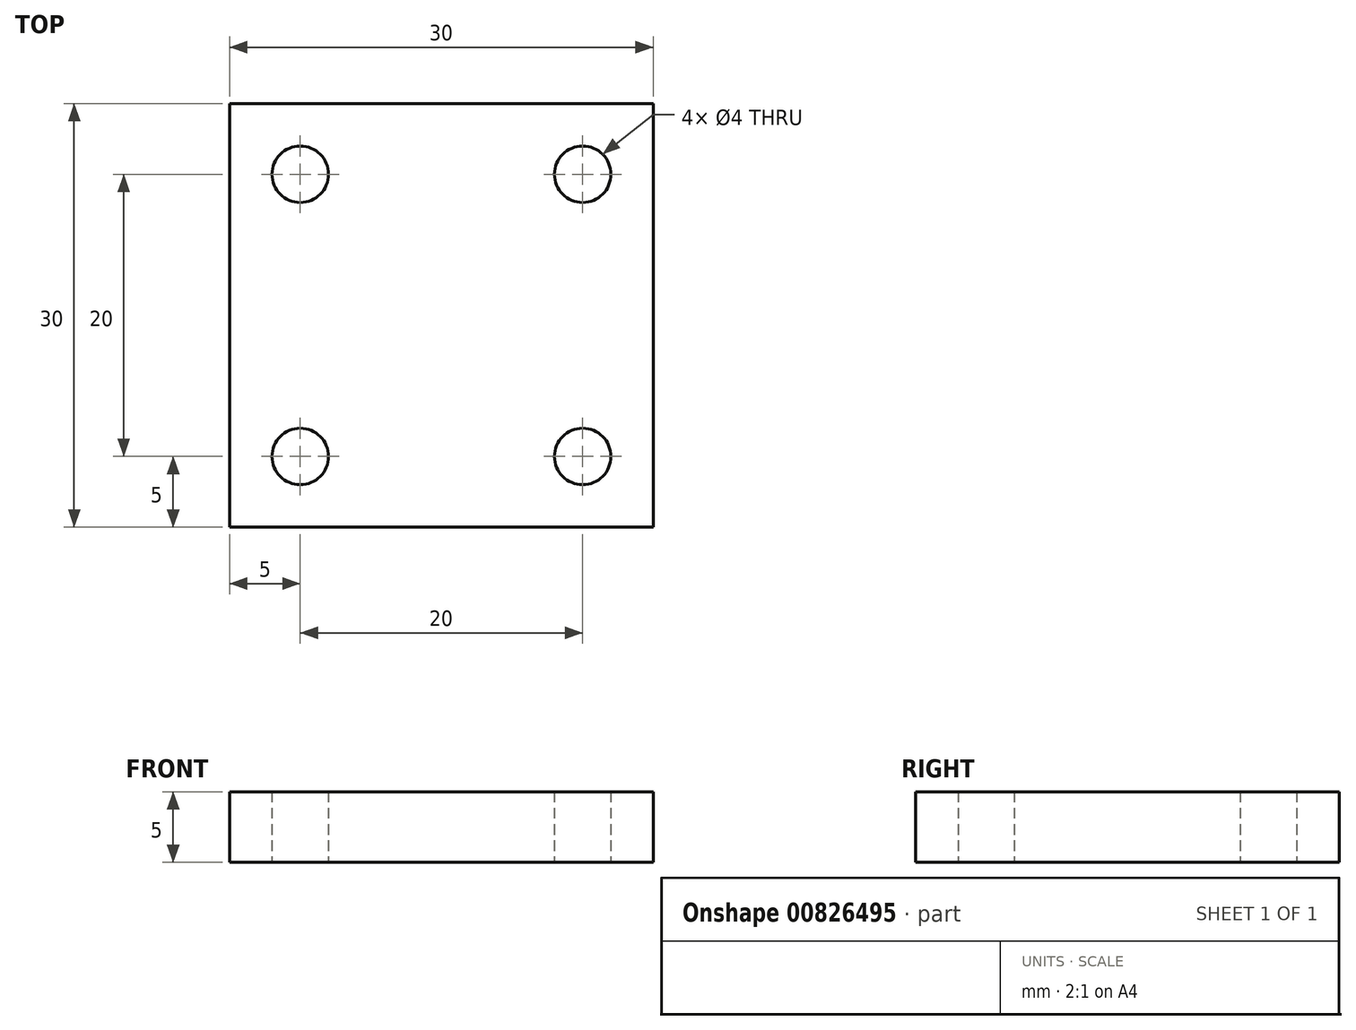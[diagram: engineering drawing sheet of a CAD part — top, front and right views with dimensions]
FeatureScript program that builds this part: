
annotation { "Feature Type Name" : "Feature", "Feature Type Description" : "" }
export const myFeature = defineFeature(function(context is Context, id is Id, definition is map)
    precondition{}
    {
        {
            var Q0;
            Q0=qCreatedBy(makeId("Top.planeOp"),FACE);
            var sketch = newSketch(context, id + "F0", { "sketchPlane" : qUnion([Q0])});
            skLineSegment(sketch, "E0.bottom", {"start": v(-15, 15) * mm, "end": v(15, 15) * mm});
            skLineSegment(sketch, "E0.top", {"start": v(-15, -15) * mm, "end": v(15, -15) * mm});
            skLineSegment(sketch, "E0.left", {"start": v(-15, 15) * mm, "end": v(-15, -15) * mm});
            skLineSegment(sketch, "E0.right", {"start": v(15, 15) * mm, "end": v(15, -15) * mm});
            skPoint(sketch, "E0.middle", {"position": v(0, 0) * mm});
            skCircle(sketch, "E1", {"center": v(-10, 10) * mm, "radius": 2 * mm});
            skCircle(sketch, "E2", {"center": v(10, 10) * mm, "radius": 2 * mm});
            skCircle(sketch, "E3", {"center": v(-10, -10) * mm, "radius": 2 * mm});
            skCircle(sketch, "E4", {"center": v(10, -10) * mm, "radius": 2 * mm});
            skSolve(sketch);
        }
        {
            var Q0;
            Q0=makeQuery(id+"F0.imprint","IMPRINT",FACE,{"disambiguationData":[TD([[makeQuery(id+"F0.imprint","IMPRINT",EDGE,{"derivedFrom":sQuery(id+"F0.wireOp",EDGE,"E0.bottom")}),-1.0]])]});
            extrude(context, id + "F1", {"entities" : qUnion([Q0]), "depth" : 5 * mm, "offsetDistance" : 25 * mm});
        }
    });
